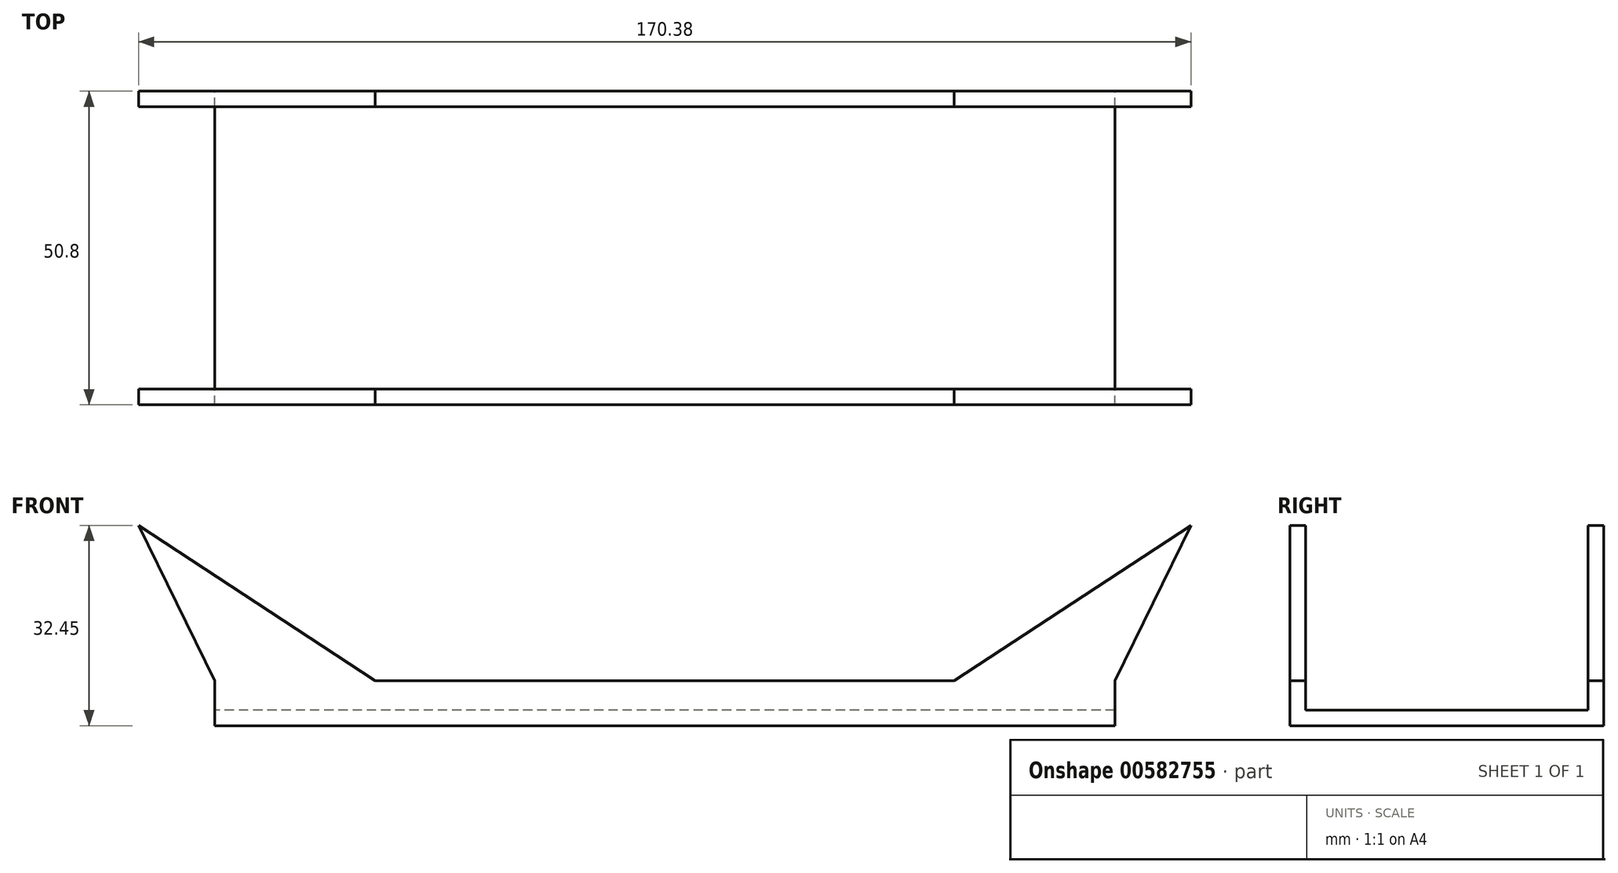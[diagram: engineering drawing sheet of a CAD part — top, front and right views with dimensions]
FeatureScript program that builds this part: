
annotation { "Feature Type Name" : "Feature", "Feature Type Description" : "" }
export const myFeature = defineFeature(function(context is Context, id is Id, definition is map)
    precondition{}
    {
        {
            var Q0;
            Q0=qCreatedBy(makeId("Front.planeOp"),FACE);
            var sketch = newSketch(context, id + "F0", { "sketchPlane" : qUnion([Q0])});
            skLineSegment(sketch, "E0", {"start": v(-72.88, 9.93) * mm, "end": v(48.82, 9.93) * mm});
            skLineSegment(sketch, "E1", {"start": v(48.82, 9.93) * mm, "end": v(48.82, 2.66) * mm});
            skLineSegment(sketch, "E2", {"start": v(48.82, 2.66) * mm, "end": v(-72.88, 2.66) * mm});
            skLineSegment(sketch, "E3", {"start": v(-72.88, 9.93) * mm, "end": v(-72.88, 2.66) * mm});
            skLineSegment(sketch, "E4", {"start": v(-72.88, 9.93) * mm, "end": v(-85.19, 35.1) * mm});
            skLineSegment(sketch, "E5", {"start": v(-85.19, 35.1) * mm, "end": v(-46.86, 9.93) * mm});
            skSolve(sketch);
        }
        {
            var Q0;
            {var subQ0=sQuery(id+"F0.wireOp",EDGE,"E4");Q0=makeQuery(id+"F0.imprint","IMPRINT",FACE,{"disambiguationData":[TD([[makeQuery(id+"F0.imprint","IMPRINT",EDGE,{"derivedFrom":subQ0}),-1.0]])]});}
            extrude(context, id + "F1", {"entities" : qUnion([Q0]), "depth" : 50.8 * mm, "offsetDistance" : 25.4 * mm});
        }
        {
            var Q0;
            {var subQ0=sQuery(id+"F0.wireOp",EDGE,"E1");Q0=makeQuery(id+"F0.imprint","IMPRINT",FACE,{"disambiguationData":[TD([[makeQuery(id+"F0.imprint","IMPRINT",EDGE,{"derivedFrom":subQ0}),-1.0]])]});}
            extrude(context, id + "F2", {"entities" : qUnion([Q0]), "operationType" : NewBodyOperationType.ADD, "depth" : 50.8 * mm, "offsetDistance" : 25.4 * mm});
        }
        {
            var Q0;
            Q0=makeQuery(id+"F1.opExtrude","SWEPT_BODY",BODY,{"disambiguationData":[OSD([sQuery(id+"F0.wireOp",EDGE,"E0"),sQuery(id+"F0.wireOp",EDGE,"E4"),sQuery(id+"F0.wireOp",EDGE,"E5")])]});
            var Q1;
            Q1=qCreatedBy(makeId("Right.planeOp"),FACE);
            mirror(context, id + "F3", {"operationType" : NewBodyOperationType.ADD, "entities" : qUnion([Q0]), "mirrorPlane" : qUnion([Q1])});
        }
        {
            var Q0;
            Q0=makeQuery(id+"F1.opExtrude","SWEPT_FACE",FACE,{"disambiguationData":[OSD([sQuery(id+"F0.wireOp",EDGE,"E5")])]});
            var Q1;
            Q1=makeQuery(id+"F3.opPattern","COPY",FACE,{"derivedFrom":makeQuery(id+"F1.opExtrude","SWEPT_FACE",FACE,{"disambiguationData":[OSD([sQuery(id+"F0.wireOp",EDGE,"E4")])]}),"instanceName":"1"});
            var Q2;
            Q2=makeQuery(id+"F3.opPattern","COPY",FACE,{"derivedFrom":makeQuery(id+"F1.opExtrude","SWEPT_FACE",FACE,{"disambiguationData":[OSD([sQuery(id+"F0.wireOp",EDGE,"E5")])]}),"instanceName":"1"});
            var Q3;
            Q3=makeQuery(id+"F1.opExtrude","SWEPT_FACE",FACE,{"disambiguationData":[OSD([sQuery(id+"F0.wireOp",EDGE,"E4")])]});
            var Q4;
            Q4=makeQuery(id+"F2.opExtrude","SWEPT_FACE",FACE,{"disambiguationData":[OSD([sQuery(id+"F0.wireOp",EDGE,"E0")])]});
            var Q5;
            Q5=makeQuery(id+"F3.opPattern","COPY",FACE,{"derivedFrom":makeQuery(id+"F2.opExtrude","SWEPT_FACE",FACE,{"disambiguationData":[OSD([sQuery(id+"F0.wireOp",EDGE,"E3")])]}),"instanceName":"1"});
            var Q6;
            Q6=makeQuery(id+"F2.opExtrude","SWEPT_FACE",FACE,{"disambiguationData":[OSD([sQuery(id+"F0.wireOp",EDGE,"E3")])]});
            shell(context, id + "F4", {"entities" : qUnion([Q0, Q1, Q2, Q3, Q4, Q5, Q6]), "thickness" : 2.54 * mm});
        }
    });
